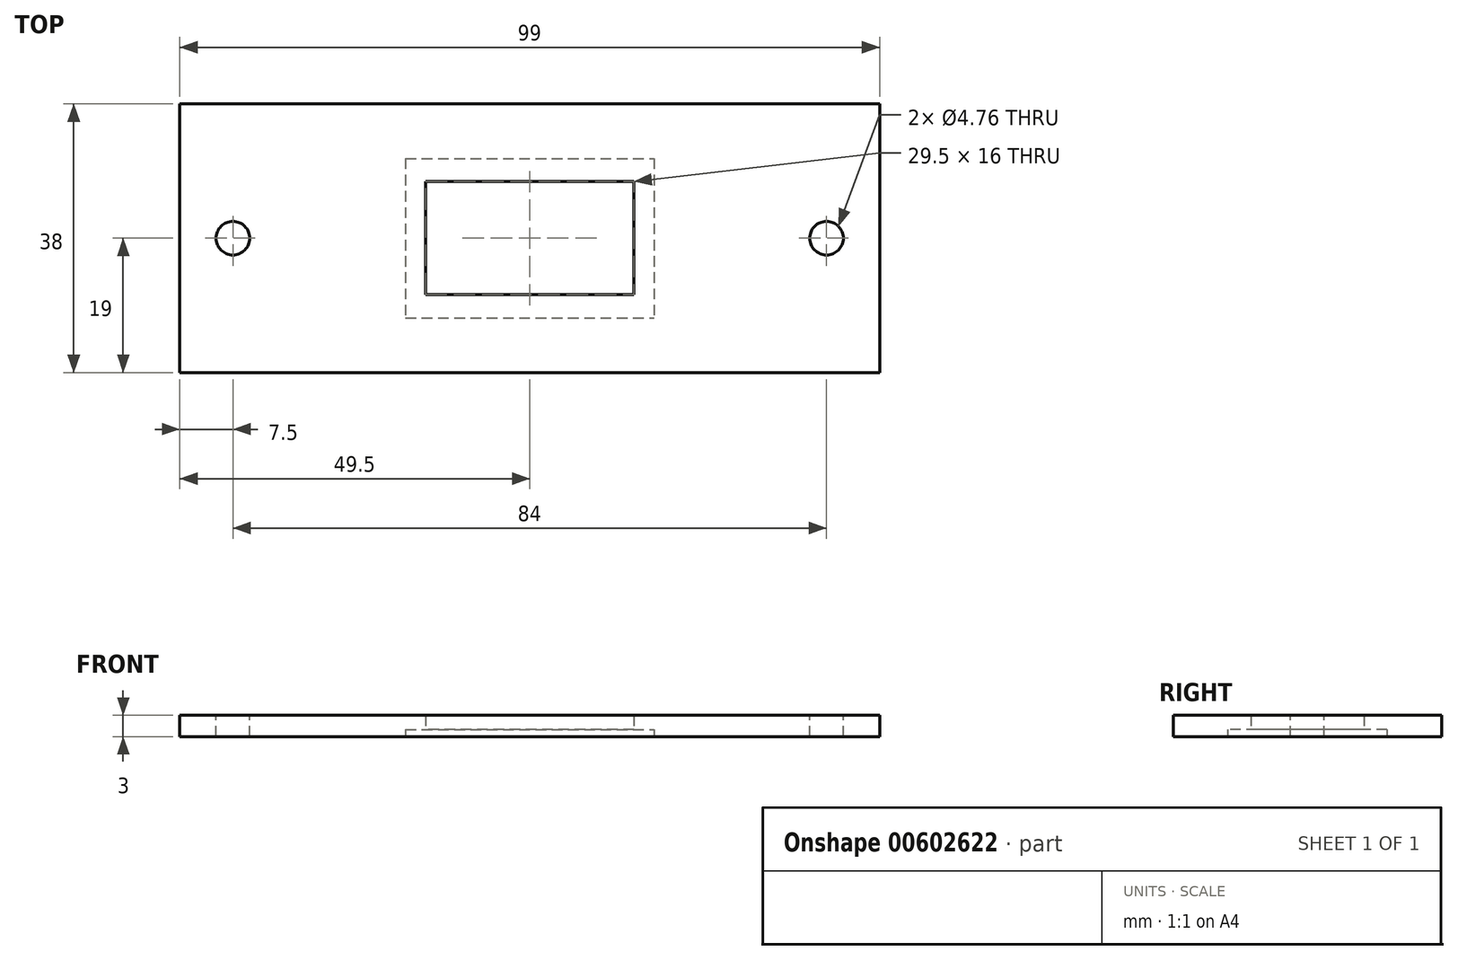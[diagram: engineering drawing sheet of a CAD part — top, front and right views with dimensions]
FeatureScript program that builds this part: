
annotation { "Feature Type Name" : "Feature", "Feature Type Description" : "" }
export const myFeature = defineFeature(function(context is Context, id is Id, definition is map)
    precondition{}
    {
        {
            var Q0;
            Q0=qCreatedBy(makeId("Top.planeOp"),FACE);
            var sketch = newSketch(context, id + "F0", { "sketchPlane" : qUnion([Q0])});
            skLineSegment(sketch, "E0.0", {"start": v(99, 0) * mm, "end": v(99, 38) * mm});
            skLineSegment(sketch, "E0.2", {"start": v(0, 0) * mm, "end": v(0, 38) * mm});
            skLineSegment(sketch, "E0.3", {"start": v(0, 38) * mm, "end": v(99, 38) * mm});
            skLineSegment(sketch, "E1", {"start": v(0, 0) * mm, "end": v(99, 0) * mm});
            skLineSegment(sketch, "E2.bottom", {"start": v(34.75, 11) * mm, "end": v(64.25, 11) * mm});
            skLineSegment(sketch, "E2.top", {"start": v(34.75, 27) * mm, "end": v(64.25, 27) * mm});
            skLineSegment(sketch, "E2.left", {"start": v(34.75, 11) * mm, "end": v(34.75, 27) * mm});
            skLineSegment(sketch, "E2.right", {"start": v(64.25, 11) * mm, "end": v(64.25, 27) * mm});
            skLineSegment(sketch, "E3", {"start": v(49.5, 11) * mm, "end": v(49.5, 0) * mm, "construction": true});
            skPoint(sketch, "E3.endSnap0", {"position": v(49.5, 11) * mm});
            skLineSegment(sketch, "E4", {"start": v(0, 19) * mm, "end": v(34.75, 19) * mm, "construction": true});
            skLineSegment(sketch, "E5", {"start": v(49.5, 27) * mm, "end": v(49.5, 38) * mm, "construction": true});
            skLineSegment(sketch, "E6", {"start": v(99, 19) * mm, "end": v(64.25, 19) * mm, "construction": true});
            skSolve(sketch);
        }
        {
            var Q0;
            Q0=qSketchRegion(id+"F0",true);
            extrude(context, id + "F1", {"entities" : qUnion([Q0]), "depth" : 3 * mm, "offsetDistance" : 25 * mm});
        }
        {
            var Q0;
            Q0=makeQuery(id+"F1.opExtrude","CAP_FACE",FACE,{"disambiguationData":[OSD([sQuery(id+"F0.wireOp",EDGE,"AiZ4gYoa-msa6-boio-fEdS-XP4aReER9jLD.bottom"),sQuery(id+"F0.wireOp",EDGE,"AiZ4gYoa-msa6-boio-fEdS-XP4aReER9jLD.top"),sQuery(id+"F0.wireOp",EDGE,"AiZ4gYoa-msa6-boio-fEdS-XP4aReER9jLD.left"),sQuery(id+"F0.wireOp",EDGE,"AiZ4gYoa-msa6-boio-fEdS-XP4aReER9jLD.right"),sQuery(id+"F0.wireOp",EDGE,"E0.0"),sQuery(id+"F0.wireOp",EDGE,"E0.1"),sQuery(id+"F0.wireOp",EDGE,"E0.2"),sQuery(id+"F0.wireOp",EDGE,"E0.3")])],"isStart":false});
            var sketch = newSketch(context, id + "F2", { "sketchPlane" : qUnion([Q0])});
            skPoint(sketch, "E7.0", {"position": v(15, 19) * mm});
            skPoint(sketch, "E8.0", {"position": v(84, 19) * mm});
            skPoint(sketch, "E9.0", {"position": v(0, 19) * mm});
            skPoint(sketch, "E10.0", {"position": v(99, 19) * mm});
            skLineSegment(sketch, "E11", {"start": v(0, 19) * mm, "end": v(15, 19) * mm, "construction": true});
            skLineSegment(sketch, "E12", {"start": v(84, 19) * mm, "end": v(99, 19) * mm, "construction": true});
            skCircle(sketch, "E13", {"center": v(7.5, 19) * mm, "radius": 2.38 * mm});
            skCircle(sketch, "E14", {"center": v(91.5, 19) * mm, "radius": 2.38 * mm});
            skSolve(sketch);
        }
        {
            var Q0;
            Q0=qSketchRegion(id+"F2",true);
            extrude(context, id + "F3", {"entities" : qUnion([Q0]), "operationType" : NewBodyOperationType.REMOVE, "endBound" : BoundingType.THROUGH_ALL, "oppositeDirection" : true, "depth" : 25 * mm, "offsetDistance" : 25 * mm});
        }
        {
            var Q0;
            Q0=makeQuery(id+"F1.opExtrude","CAP_FACE",FACE,{"disambiguationData":[OSD([sQuery(id+"F0.wireOp",EDGE,"E0.0"),sQuery(id+"F0.wireOp",EDGE,"E0.2"),sQuery(id+"F0.wireOp",EDGE,"E0.3"),sQuery(id+"F0.wireOp",EDGE,"E1"),sQuery(id+"F0.wireOp",EDGE,"E2.bottom"),sQuery(id+"F0.wireOp",EDGE,"E2.top"),sQuery(id+"F0.wireOp",EDGE,"E2.left"),sQuery(id+"F0.wireOp",EDGE,"E2.right")])],"isStart":true});
            var sketch = newSketch(context, id + "F4", { "sketchPlane" : qUnion([Q0])});
            skLineSegment(sketch, "E15.bottom", {"start": v(31.92, -30.28) * mm, "end": v(67.07, -30.28) * mm});
            skLineSegment(sketch, "E15.top", {"start": v(31.92, -7.73) * mm, "end": v(67.07, -7.73) * mm});
            skLineSegment(sketch, "E15.left", {"start": v(31.92, -30.28) * mm, "end": v(31.92, -7.73) * mm});
            skLineSegment(sketch, "E15.right", {"start": v(67.07, -30.28) * mm, "end": v(67.07, -7.73) * mm});
            skLineSegment(sketch, "E16.0", {"start": v(0, 0) * mm, "end": v(99, 0) * mm, "construction": true});
            skLineSegment(sketch, "E17.0", {"start": v(0, 0) * mm, "end": v(0, -38) * mm, "construction": true});
            skLineSegment(sketch, "E18", {"start": v(0, -19) * mm, "end": v(31.92, -19) * mm, "construction": true});
            skLineSegment(sketch, "E19", {"start": v(67.07, -19) * mm, "end": v(99, -19) * mm, "construction": true});
            skLineSegment(sketch, "E20", {"start": v(49.5, 0) * mm, "end": v(49.5, -7.73) * mm, "construction": true});
            skLineSegment(sketch, "E21", {"start": v(49.5, -30.28) * mm, "end": v(49.5, -38) * mm, "construction": true});
            skSolve(sketch);
        }
        {
            var Q0;
            Q0 = qSketchRegion(id + "F4", true);
            extrude(context, id + "F5", {"entities" : qUnion([Q0]), "operationType" : NewBodyOperationType.REMOVE, "oppositeDirection" : true, "depth" : 1 * mm, "offsetDistance" : 25 * mm});
        }
    });
